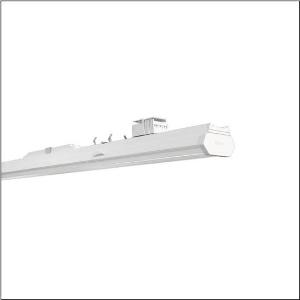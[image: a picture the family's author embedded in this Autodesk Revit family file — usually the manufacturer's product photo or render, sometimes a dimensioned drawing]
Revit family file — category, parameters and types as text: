
# Revit family: licross_r__11_protected_extreme_mo_51td1bdn49xge_f438
name_source: partatom
category: Lighting Fixtures
units: mm (PartAtom-declared; Revit-internal decimal feet)

## family parameters
Cut with Voids When Loaded = No
Host = Face
Light Source = No
Part Type = Normal
Room Calculation Point = No
Round Connector Dimension = Use Diameter
Shared = No

## types (1)
- --- (1 x LED, 9370 lm, 57.1 W, 4000K)
    Apparent Load = 57 VA
    CIE Flux Codes = 54 82 95 97 100
    Color Rendering = 80
    Color Temperature = 4000K
    Default Elevation = 1800 mm
    Description = Licross® 11 Protected extreme MO, luminaire insert, of sheet steel, galvanised, coil coated, white, length: 1.500mm, width: 90mm, height: 101mm, LED rated luminous flux: 9.370lm, light colour: 840, control gear: DALI 2, with plug, 5-pole, with phase selection, mains connection: 220..240V, AC, 50/60Hz, rated input power: 57W, halogen-free wiring, primary optical cover: cover, of PMMA, light emission: direct distribution, primary light characteristic: symmetric, protection rating (complete): IP54, insulation class (complete): insulation class I (protective earthing), certification: CE, ENEC, VDE, UKCA, protection symbol: D if used in an environment with non-conductive dust loads with corresponding accessories, impact resistance: IK06, permissible ambient temperature for indoor applications: -40..+35°C, corresponds to IFS (International Featured Standards) requirements for safety and quality in the food industry, reducing of maximum allowable ambient temperature of 5°C with ceiling mounting, LABS conformity tested according to VDMA 24364:2018-05, packaging unit: 1 piece
    Height = 92 mm
    Lamp = 1 x LED
    Lamp Light Flux = 9370 lm
    Lamp Power = 57.1 W
    Lamp count = 1
    Length = 1500 mm
    Luminous efficacy = 164 lm/W
    Manufacturer = Siteco
    ModVariant = No
    Model = 51TD1BDN49XGE
    Mounting Place = Ceiling
    Mounting Type = Pendant
    Number of Poles = 1
    OnlyDefault = Yes
    Power Factor = 1
    Product Name = Licross® 11 Protected extreme MO
    Product group = luminaire insert
    ProductGroupID = 901
    Protection Class = Protection class I
    Protection Degree = IP 54
    RLX_Detail_Level = 1
    RLX_Emergency_Light_Flux = 0 lm
    RLX_Emergency_Type = 0
    RLX_Emergency_Type_DB = No
    RlxData = <blob elided: 24281 chars, md5=1303b17d>
    Socket = socket
    Standby Power = 0 W
    System Light Flux = 9370 lm
    System Power = 57 W
    Type Comments = factory setting: luminous flux: 100 % | dim-lin: 254 | 378 mA
    Type Image = l_1256145.jpg
    URL = http://relux.com
    VarID = @adj_052063
    Voltage = 0 V
    Weight = 0.00 kg
    Width = 88 mm

## geometry (parser evidence)
native form markers: Blend x4, Sweep x10
no freeform markers — native parametric forms only
